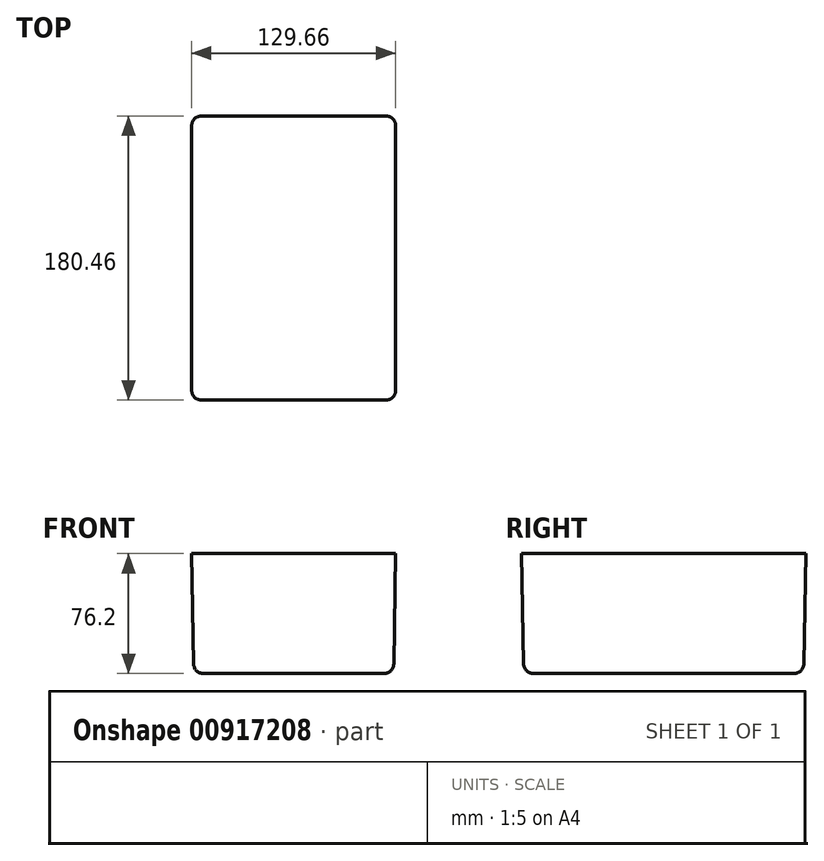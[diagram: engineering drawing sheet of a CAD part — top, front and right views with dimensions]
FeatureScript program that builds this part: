
annotation { "Feature Type Name" : "Feature", "Feature Type Description" : "" }
export const myFeature = defineFeature(function(context is Context, id is Id, definition is map)
    precondition{}
    {
        {
            var Q0;
            Q0=qCreatedBy(makeId("Top.planeOp"),FACE);
            var sketch = newSketch(context, id + "F0", { "sketchPlane" : qUnion([Q0])});
            skLineSegment(sketch, "E0.bottom", {"start": v(63.5, -88.9) * mm, "end": v(-63.5, -88.9) * mm});
            skLineSegment(sketch, "E0.top", {"start": v(63.5, 88.9) * mm, "end": v(-63.5, 88.9) * mm});
            skLineSegment(sketch, "E0.left", {"start": v(63.5, -88.9) * mm, "end": v(63.5, 88.9) * mm});
            skLineSegment(sketch, "E0.right", {"start": v(-63.5, -88.9) * mm, "end": v(-63.5, 88.9) * mm});
            skPoint(sketch, "E0.middle", {"position": v(0, 0) * mm});
            skSolve(sketch);
        }
        {
            var Q0;
            Q0 = qSketchRegion(id + "F0", true);
            extrude(context, id + "F1", {"entities" : qUnion([Q0]), "depth" : 76.2 * mm, "offsetDistance" : 25.4 * mm, "hasDraft" : true, "draftAngle" : 1 * degree});
        }
        {
            var Q0;
            Q0=makeQuery(id+"F1.opExtrude","SWEPT_EDGE",EDGE,{"disambiguationData":[OSD([sQuery(id+"F0.wireOp",EDGE,"E0.top"),sQuery(id+"F0.wireOp",EDGE,"E0.right")])]});
            var Q1;
            Q1=makeQuery(id+"F1.opExtrude","SWEPT_EDGE",EDGE,{"disambiguationData":[OSD([sQuery(id+"F0.wireOp",EDGE,"E0.top"),sQuery(id+"F0.wireOp",EDGE,"E0.left")])]});
            var Q2;
            Q2=makeQuery(id+"F1.opExtrude","SWEPT_EDGE",EDGE,{"disambiguationData":[OSD([sQuery(id+"F0.wireOp",EDGE,"E0.bottom"),sQuery(id+"F0.wireOp",EDGE,"E0.left")])]});
            var Q3;
            Q3=makeQuery(id+"F1.opExtrude","SWEPT_EDGE",EDGE,{"disambiguationData":[OSD([sQuery(id+"F0.wireOp",EDGE,"E0.bottom"),sQuery(id+"F0.wireOp",EDGE,"E0.right")])]});
            fillet(context, id + "F2", {"entities" : qUnion([Q0, Q1, Q2, Q3]), "radius" : 6.35 * mm, "tangentPropagation" : true, "allowEdgeOverflow" : false});
        }
        {
            var Q0;
            Q0=makeQuery(id+"F1.opExtrude","CAP_EDGE",EDGE,{"disambiguationData":[OSD([sQuery(id+"F0.wireOp",EDGE,"E0.left")])],"isStart":true});
            fillet(context, id + "F3", {"entities" : qUnion([Q0]), "radius" : 6.35 * mm, "tangentPropagation" : true, "allowEdgeOverflow" : false});
        }
    });
